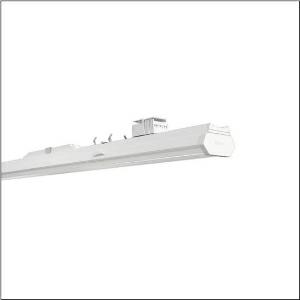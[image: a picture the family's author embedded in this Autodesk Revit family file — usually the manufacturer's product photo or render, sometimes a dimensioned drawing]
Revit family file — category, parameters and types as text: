
# Revit family: licross_r__21_protected_mo_52tp12dn4a5gd_0331
name_source: partatom
category: Lighting Fixtures
units: mm (PartAtom-declared; Revit-internal decimal feet)

## family parameters
Cut with Voids When Loaded = No
Host = Face
Light Source = No
Part Type = Normal
Room Calculation Point = No
Round Connector Dimension = Use Diameter
Shared = No

## types (1)
- --- (1 x LED, 1610 lm, 10.2 W, 4000K)
    Apparent Load = 10 VA
    CIE Flux Codes = 73 92 98 99 100
    Color Rendering = 80
    Color Temperature = 4000K
    Default Elevation = 1800 mm
    Description = Licross® 21 Protected MO, luminaire insert, of sheet steel, galvanised, coil coated, white, length: 1.500mm, width: 90mm, height: 103mm, LED rated luminous flux: 10.700lm, light colour: 840, control gear: DALI 2 (for two DALI lines), with plug, 6-pole, with phase selection, mains connection: 220..240V, AC/DC, 0/50..60Hz, rated input power: 62W, without changeover relay, for emergency light function, for central battery installations according to DIN EN 60598-2-22, internal wiring halogen-free, primary light control with lens, of plastic, primary optical cover: cover, of PMMA, light emission: direct distribution, primary light characteristic: symmetric, protection rating (complete): IP64, insulation class (complete): insulation class I (protective earthing), certification: CE, ENEC, VDE, UKCA, protection symbol: D if used in an environment with conductive dust loads with corresponding accessories, impact resistance: IK06, permissible ambient temperature for indoor applications: -25..+35°C, standard: EN 60598-2-22, corresponds to IFS (International Featured Standards) requirements for safety and quality in the food industry, reducing of maximum allowable ambient temperature of 5°C with ceiling mounting, LABS conformity tested according to VDMA 24364:2018-05, packaging unit: 1 piece
    Height = 92 mm
    Lamp = 1 x LED
    Lamp Light Flux = 1610 lm
    Lamp Power = 10.2 W
    Lamp count = 1
    Length = 1500 mm
    Luminous efficacy = 158 lm/W
    Manufacturer = Siteco
    ModVariant = No
    Model = 52TP12DN4A5GD
    Mounting Place = Ceiling
    Mounting Type = Pendant
    Number of Poles = 1
    OnlyDefault = Yes
    Power Factor = 1
    Product Name = Licross® 21 Protected MO
    Product group = luminaire insert | ceiling pendant
    ProductGroupID = 902
    Protection Class = Protection class I
    Protection Degree = IP 64
    RLX_Detail_Level = 1
    RLX_Emergency_Light_Flux = 0 lm
    RLX_Emergency_Type = 0
    RLX_Emergency_Type_DB = No
    RlxData = <blob elided: 25037 chars, md5=6184ae84>
    Socket = socket
    Standby Power = 0 W
    System Light Flux = 1610 lm
    System Power = 10 W
    Type Comments = : DC mode (central or group accumulator) initial emergency light level
    Type Image = l_1256148.jpg
    URL = http://relux.com
    VarID = @adj_137779
    Voltage = 0 V
    Weight = 0.00 kg
    Width = 88 mm

## geometry (parser evidence)
native form markers: Blend x4, Sweep x9
no freeform markers — native parametric forms only
